# Revit family: Faucet-Lavatory-KOHLER-ARTIFACTS-K-72762T
name_source: partatom
category: Plumbing Fixtures
revit_build: Autodesk Revit 2017 (Build: 20160225_1515(x64)
units: mm (PartAtom-declared; Revit-internal decimal feet)

## family parameters
Cut with Voids When Loaded = No
Host = Face
OmniClass Number = 23.31.11.00
OmniClass Title = Faucets
Part Type = Normal
Room Calculation Point = No
Round Connector Dimension = Use Diameter
Shared = No

## types (13) — shared parameters
ADA Compliant = No
Assembly Code = D2010
CW Connection = Yes
Cold Water Inlet = Cold Water Inlet
Date Modified = 09/11/2020
Default Elevation = 36"
Drain Included = No
Faucet Hole Spacing = 0"
Flow Rate = 2 GPM
HW Connection = Yes
Handle Clearance = 2 3/4"
Height = 6 15/16"
Hot Water Inlet = Hot Water Inlet
Length = 5 11/16"
Manufacturer = KOHLER Co.
Master Format 2014 = 22 41 39
Master Format 2014 Name = Residential Faucets, Supplies, and Trim
Material = Premium Metal Construction
Pressure = 60.00 psi
Product Name = ARTIFACTS
Spout Reach = 5 11/16"
URL = http://www.kohler.com.cn
Vent Connection = No
Waste Connection = No
Waste Water Outlet = Waste Water Outlet
WaterSense Certified = No
Width = 2 11/16"

## per-type parameters (varying)
| type | Description | Finish | Model | Product Documentation Link | Product Page URL | Type |
| CP-Polished Chrome | ARTIFACTS® single lever washbasin mixer | Kohler-Metal-CP-Polished_Chrome | K-72762T-9M-CP | https://files.kohler.com.cn | https://www.kohler.com.cn | 1 |
| BV-Roman Copper | ARTIFACTS® single lever washbasin mixer | Kohler-Metal-BV-Roman_Copper | K-72762-9M-BV | https://files.kohler.com.cn | https://www.kohler.com.cn | 2 |
| RGD-Rose Gold | ARTIFACTS® single lever washbasin mixer | Kohler-Metal-RGD-Rose_Gold | K-72762T-9M-RGD | https://files.kohler.com.cn | https://www.kohler.com.cn | 3 |
| 2BZ-Elegant Black | ARTIFACTS® single lever washbasin mixer | Kohler-Metal-2BZ-Elegant_Black | K-72762T-9M-2BZ | https://files.kohler.com.cn | https://www.kohler.com.cn | 4 |
| AF-Flange Gold | ARTIFACTS® single lever washbasin mixer | Kohler-Metal-AF-Flange_Gold | K-72762T-9M-AF | https://files.kohler.com.cn | https://www.kohler.com.cn | 5 |
| BN-Roman Silver | ARTIFACTS® single lever washbasin mixer | Kohler-Metal-BN-Roman_Silver | K-72762T-9M-BN | https://files.kohler.com.cn | https://www.kohler.com.cn | 6 |
| SN-Champagne Gold | ARTIFACTS® single lever washbasin mixer | Kohler-Metal-SN-Champagne_Gold | K-72762T-9M-SN | https://files.kohler.com.cn | https://www.kohler.com.cn | 7 |
| PGD-Eternal Gold | ARTIFACTS® single lever washbasin mixer | Kohler-Metal-PGD-Eternal_Gold | K-72762T-9M-SN | https://files.kohler.com.cn | https://www.kohler.com.cn | 7 |
| TT-Titanium Silver | ARTIFACTS® single lever washbasin mixer | Kohler-Metal-TT-Titanium_Silver | K-72762T-9M-TT | https://files.kohler.com.cn | https://www.kohler.com.cn | 9 |
| 2BL-Original Black | ARTIFACTS® single lever washbasin mixer | Kohler-Metal-2BL-Original_Black | K-72762T-9M-2BL | https://files.kohler.com.cn | https://www.kohler.com.cn | 10 |
| 9MND-CP-Polished Chrome | ARTIFACTS SINGLE-HANDLE LAV FAUCET | Kohler-Metal-CP-Polished_Chrome | K-72762T-9MND-CP |  |  | 11 |
| 9MND-BV-Roman Copper | ARTIFACTS SINGLE-HANDLE LAV FAUCET | Kohler-Metal-BV-Roman_Copper | K-72762T-9MND-BV |  |  | 12 |
| 9MND-2BZ-Elegant Black | ARTIFACTS SINGLE-HANDLE LAV FAUCET | Kohler-Metal-2BZ-Elegant_Black | K-72762T-9MND-2BZ |  |  | 13 |

## geometry (parser evidence)
native form markers: Sweep x4
no freeform markers — native parametric forms only
